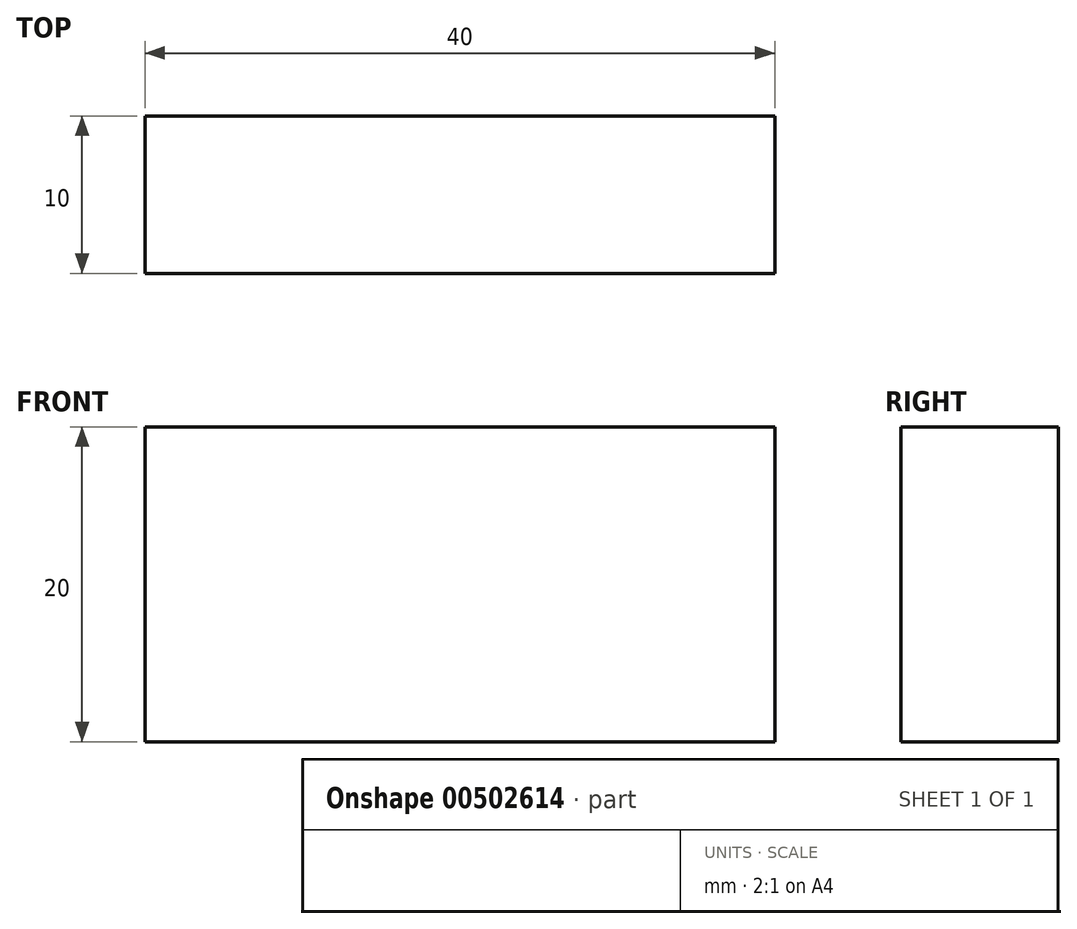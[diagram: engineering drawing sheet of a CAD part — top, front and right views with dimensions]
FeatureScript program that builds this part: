
annotation { "Feature Type Name" : "Feature", "Feature Type Description" : "" }
export const myFeature = defineFeature(function(context is Context, id is Id, definition is map)
    precondition{}
    {
        {
            var Q0;
            Q0=qCreatedBy(makeId("Front.planeOp"),FACE);
            var sketch = newSketch(context, id + "F0", { "sketchPlane" : qUnion([Q0])});
            skLineSegment(sketch, "E0.bottom", {"start": v(-7.5, 1.83) * mm, "end": v(32.5, 1.83) * mm});
            skLineSegment(sketch, "E0.top", {"start": v(-7.5, -18.17) * mm, "end": v(32.5, -18.17) * mm});
            skLineSegment(sketch, "E0.left", {"start": v(-7.5, 1.83) * mm, "end": v(-7.5, -18.17) * mm});
            skLineSegment(sketch, "E0.right", {"start": v(32.5, 1.83) * mm, "end": v(32.5, -18.17) * mm});
            skSolve(sketch);
        }
        {
            var Q0;
            Q0=makeQuery(id+"F0.imprint","IMPRINT",FACE,{"disambiguationData":[TD([[makeQuery(id+"F0.imprint","IMPRINT",EDGE,{"derivedFrom":sQuery(id+"F0.wireOp",EDGE,"E0.bottom")}),-1.0]])]});
            extrude(context, id + "F1", {"entities" : qUnion([Q0]), "depth" : 10 * mm});
        }
    });
